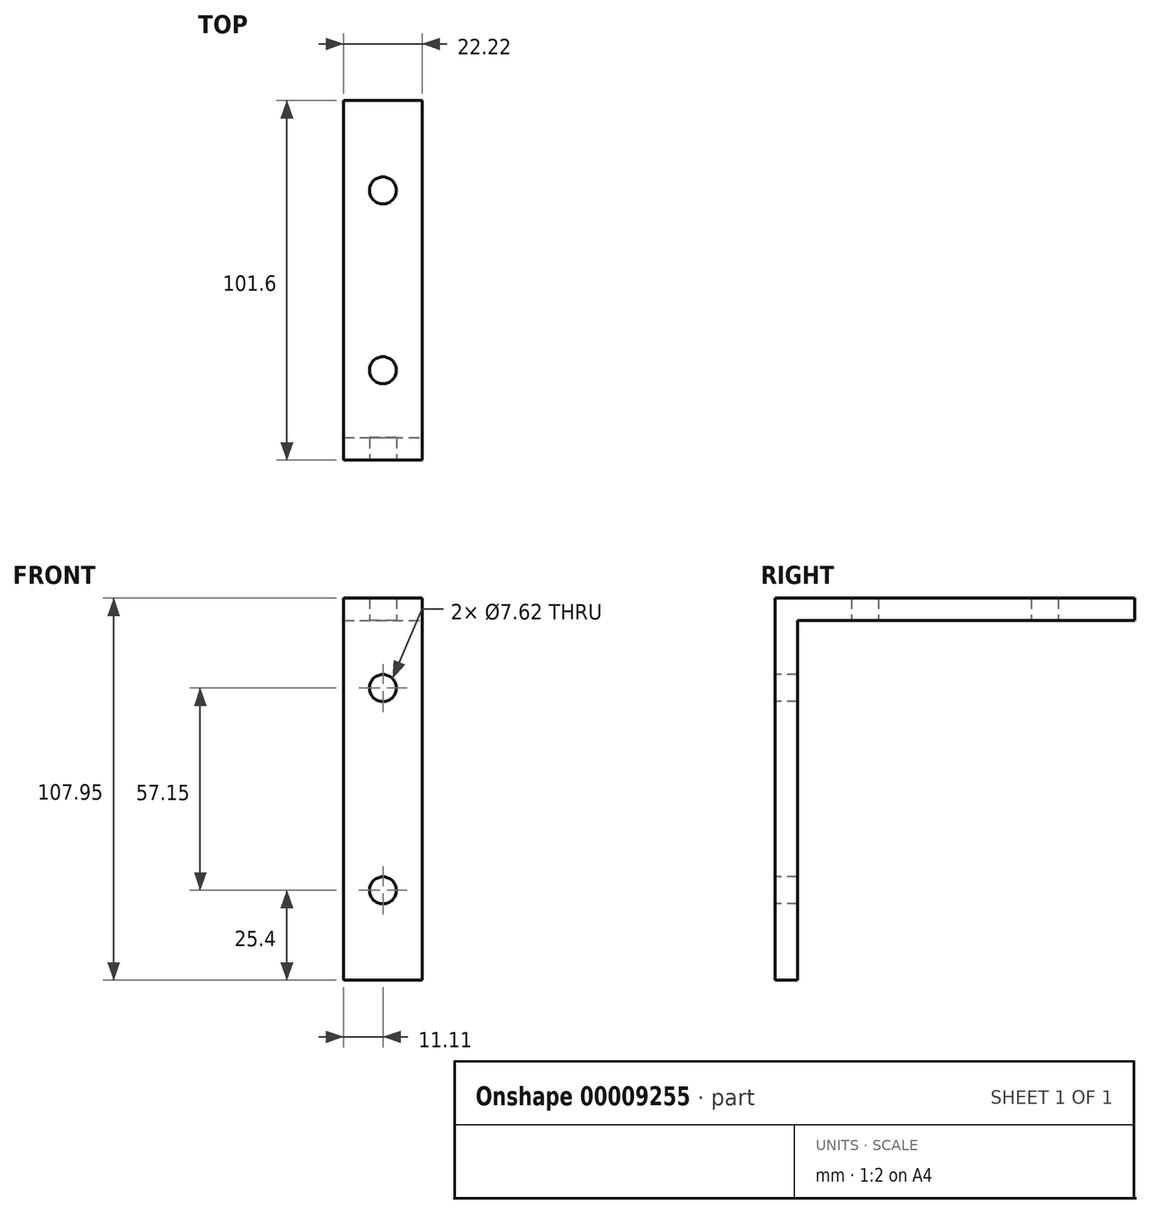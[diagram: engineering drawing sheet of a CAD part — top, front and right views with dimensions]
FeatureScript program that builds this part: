
annotation { "Feature Type Name" : "Feature", "Feature Type Description" : "" }
export const myFeature = defineFeature(function(context is Context, id is Id, definition is map)
    precondition{}
    {
        {
            var Q0;
            Q0=qCreatedBy(makeId("Top.planeOp"),FACE);
            var sketch = newSketch(context, id + "F0", { "sketchPlane" : qUnion([Q0])});
            skLineSegment(sketch, "E0.rect.bottom", {"start": v(11.11, 50.8) * mm, "end": v(-11.11, 50.8) * mm});
            skLineSegment(sketch, "E0.rect.top", {"start": v(11.11, -50.8) * mm, "end": v(-11.11, -50.8) * mm});
            skLineSegment(sketch, "E0.rect.left", {"start": v(11.11, 50.8) * mm, "end": v(11.11, -50.8) * mm});
            skLineSegment(sketch, "E0.rect.right", {"start": v(-11.11, 50.8) * mm, "end": v(-11.11, -50.8) * mm});
            skPoint(sketch, "E0.rect.middle", {"position": v(0, 0) * mm});
            skLineSegment(sketch, "E1.bottom", {"start": v(-11.11, 50.8) * mm, "end": v(5.99, 50.8) * mm});
            skLineSegment(sketch, "E1.left", {"start": v(-11.11, 50.8) * mm, "end": v(-11.11, 25.4) * mm});
            skLineSegment(sketch, "E2.bottom", {"start": v(11.11, -50.8) * mm, "end": v(-6.4, -50.8) * mm});
            skLineSegment(sketch, "E2.left", {"start": v(11.11, -50.8) * mm, "end": v(11.11, -25.4) * mm});
            skCircle(sketch, "E3", {"center": v(0, -25.4) * mm, "radius": 3.81 * mm});
            skCircle(sketch, "E4", {"center": v(0, 25.4) * mm, "radius": 3.81 * mm});
            skPoint(sketch, "E5.orphan", {"position": v(0, 50.8) * mm});
            skPoint(sketch, "E6.orphan", {"position": v(11.11, 0) * mm});
            skPoint(sketch, "E7.start.orphan", {"position": v(-11.11, 0) * mm});
            skPoint(sketch, "E8.orphan", {"position": v(0, -50.8) * mm});
            skSolve(sketch);
        }
        {
            var Q0;
            Q0=makeQuery(id+"F0.imprint","IMPRINT",FACE,{"disambiguationData":[TD([[makeQuery(id+"F0.imprint","IMPRINT",EDGE,{"derivedFrom":sQuery(id+"F0.wireOp",EDGE,"E0.rect.bottom")}),1.0]])]});
            extrude(context, id + "F1", {"entities" : qUnion([Q0]), "depth" : 6.35 * mm});
        }
        {
            var Q0;
            Q0=makeQuery(id+"F1.opExtrude","CAP_FACE",FACE,{"disambiguationData":[OSD([sQuery(id+"F0.wireOp",EDGE,"E0.rect.bottom"),sQuery(id+"F0.wireOp",EDGE,"E0.rect.top"),sQuery(id+"F0.wireOp",EDGE,"E0.rect.left"),sQuery(id+"F0.wireOp",EDGE,"E0.rect.right"),sQuery(id+"F0.wireOp",EDGE,"E1.bottom"),sQuery(id+"F0.wireOp",EDGE,"E1.left"),sQuery(id+"F0.wireOp",EDGE,"E2.bottom"),sQuery(id+"F0.wireOp",EDGE,"E2.left"),sQuery(id+"F0.wireOp",EDGE,"E3"),sQuery(id+"F0.wireOp",EDGE,"E4")])],"isStart":true});
            var sketch = newSketch(context, id + "F2", { "sketchPlane" : qUnion([Q0])});
            skLineSegment(sketch, "E9.bottom", {"start": v(-11.11, 50.8) * mm, "end": v(11.11, 50.8) * mm});
            skLineSegment(sketch, "E9.top", {"start": v(-11.11, 44.45) * mm, "end": v(11.11, 44.45) * mm});
            skLineSegment(sketch, "E9.left", {"start": v(-11.11, 50.8) * mm, "end": v(-11.11, 44.45) * mm});
            skLineSegment(sketch, "E9.right", {"start": v(11.11, 50.8) * mm, "end": v(11.11, 44.45) * mm});
            skSolve(sketch);
        }
        {
            var Q0;
            Q0=makeQuery(id+"F2.imprint","IMPRINT",FACE,{"disambiguationData":[TD([[makeQuery(id+"F2.imprint","IMPRINT",EDGE,{"derivedFrom":sQuery(id+"F2.wireOp",EDGE,"E9.bottom")}),1.0]])]});
            extrude(context, id + "F3", {"entities" : qUnion([Q0]), "operationType" : NewBodyOperationType.ADD, "depth" : 101.6 * mm});
        }
        {
            var Q0;
            Q0=makeQuery(id+"F3.boolean.opBoolean","MERGE",FACE,{"derivedFrom":[makeQuery(id+"F1.opExtrude","SWEPT_FACE",FACE,{"disambiguationData":[OSD([sQuery(id+"F0.wireOp",EDGE,"E0.rect.top"),sQuery(id+"F0.wireOp",EDGE,"E2.bottom")])]}),makeQuery(id+"F3.opExtrude","SWEPT_FACE",FACE,{"disambiguationData":[OSD([sQuery(id+"F2.wireOp",EDGE,"E9.bottom")])]})]});
            var sketch = newSketch(context, id + "F4", { "sketchPlane" : qUnion([Q0])});
            skLineSegment(sketch, "E10.top", {"start": v(3.8, -19.05) * mm, "end": v(4.15, -19.05) * mm});
            skCircle(sketch, "E11", {"center": v(0, -19.05) * mm, "radius": 3.81 * mm});
            skCircle(sketch, "E12", {"center": v(0, -76.2) * mm, "radius": 3.81 * mm});
            skPoint(sketch, "E13.orphan", {"position": v(-11.11, -47.62) * mm});
            skLineSegment(sketch, "E14.trimOffspring", {"start": v(0, -72.4) * mm, "end": v(0, -76.2) * mm});
            skPoint(sketch, "E15.trimOffspring.end.orphan", {"position": v(0, -101.6) * mm});
            skPoint(sketch, "E16.orphan", {"position": v(0, 6.35) * mm});
            skSolve(sketch);
        }
        {
            var Q0;
            Q0 = qSketchRegion(id + "F4", true);
            extrude(context, id + "F5", {"entities" : qUnion([Q0]), "operationType" : NewBodyOperationType.REMOVE, "oppositeDirection" : true, "depth" : 24.02 * mm});
        }
    });
